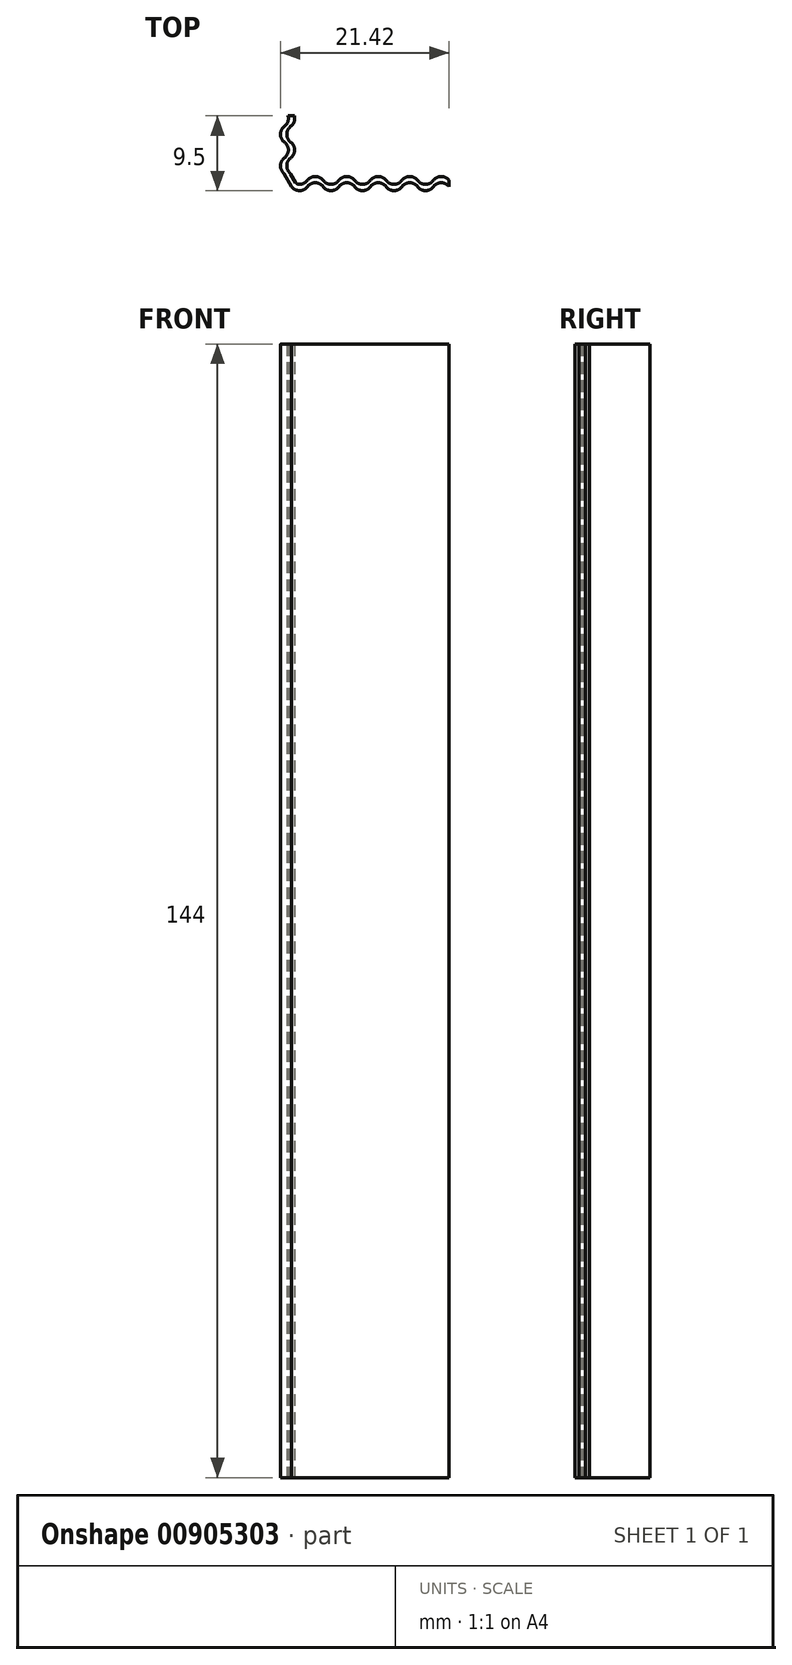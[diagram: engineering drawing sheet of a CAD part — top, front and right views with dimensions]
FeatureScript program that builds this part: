
annotation { "Feature Type Name" : "Feature", "Feature Type Description" : "" }
export const myFeature = defineFeature(function(context is Context, id is Id, definition is map)
    precondition{}
    {
        {
            var Q0;
            Q0=qCreatedBy(makeId("Top.planeOp"),FACE);
            var sketch = newSketch(context, id + "F0", { "sketchPlane" : qUnion([Q0])});
            skArc(sketch, "E0", {"start": v(-9.41, -6.92) * mm, "mid": v(-9.91, -7.92) * mm, "end": v(-9.41, -8.92) * mm});
            skArc(sketch, "E1", {"start": v(-9.41, -10.92) * mm, "mid": v(-8.91, -9.92) * mm, "end": v(-9.41, -8.92) * mm});
            skArc(sketch, "E2", {"start": v(-7.29, -13.78) * mm, "mid": v(-7.78, -14.17) * mm, "end": v(-8.4, -14.27) * mm});
            skArc(sketch, "E3", {"start": v(-8.4, -14.27) * mm, "mid": v(-8.62, -14.2) * mm, "end": v(-8.78, -14.04) * mm});
            skLineSegment(sketch, "E4", {"start": v(-8.78, -14.04) * mm, "end": v(-9.44, -12.97) * mm});
            skArc(sketch, "E5", {"start": v(-9.44, -12.97) * mm, "mid": v(-9.52, -12.85) * mm, "end": v(-9.61, -12.73) * mm});
            skArc(sketch, "E6", {"start": v(-9.61, -12.73) * mm, "mid": v(-9.9, -11.78) * mm, "end": v(-9.41, -10.92) * mm});
            skArc(sketch, "E7", {"start": v(-9.29, -14.58) * mm, "mid": v(-8.29, -15.08) * mm, "end": v(-7.29, -14.58) * mm});
            skArc(sketch, "E8", {"start": v(-5.29, -14.58) * mm, "mid": v(-6.29, -14.08) * mm, "end": v(-7.29, -14.58) * mm});
            skArc(sketch, "E9", {"start": v(-5.29, -14.58) * mm, "mid": v(-4.29, -15.08) * mm, "end": v(-3.29, -14.58) * mm});
            skArc(sketch, "E10", {"start": v(-1.29, -14.58) * mm, "mid": v(-2.29, -14.08) * mm, "end": v(-3.29, -14.58) * mm});
            skArc(sketch, "E11", {"start": v(-1.29, -14.58) * mm, "mid": v(-0.29, -15.08) * mm, "end": v(0.71, -14.58) * mm});
            skArc(sketch, "E12", {"start": v(2.71, -14.58) * mm, "mid": v(1.71, -14.08) * mm, "end": v(0.71, -14.58) * mm});
            skArc(sketch, "E13", {"start": v(10.71, -14.58) * mm, "mid": v(9.71, -14.08) * mm, "end": v(8.71, -14.58) * mm});
            skArc(sketch, "E14", {"start": v(6.71, -14.58) * mm, "mid": v(7.71, -15.08) * mm, "end": v(8.71, -14.58) * mm});
            skArc(sketch, "E15", {"start": v(6.71, -14.58) * mm, "mid": v(5.71, -14.08) * mm, "end": v(4.71, -14.58) * mm});
            skArc(sketch, "E16", {"start": v(2.71, -14.58) * mm, "mid": v(3.71, -15.08) * mm, "end": v(4.71, -14.58) * mm});
            skArc(sketch, "E17", {"start": v(-9.41, 13.08) * mm, "mid": v(-8.91, 14.08) * mm, "end": v(-9.41, 15.08) * mm});
            skArc(sketch, "E18", {"start": v(-9.41, 13.08) * mm, "mid": v(-9.91, 12.08) * mm, "end": v(-9.41, 11.08) * mm});
            skArc(sketch, "E19", {"start": v(-9.41, 9.08) * mm, "mid": v(-8.91, 10.08) * mm, "end": v(-9.41, 11.08) * mm});
            skArc(sketch, "E20", {"start": v(-9.41, 9.08) * mm, "mid": v(-9.91, 8.08) * mm, "end": v(-9.41, 7.08) * mm});
            skArc(sketch, "E21", {"start": v(-9.41, 5.08) * mm, "mid": v(-8.91, 6.08) * mm, "end": v(-9.41, 7.08) * mm});
            skArc(sketch, "E22", {"start": v(-9.41, 5.08) * mm, "mid": v(-9.91, 4.08) * mm, "end": v(-9.41, 3.08) * mm});
            skArc(sketch, "E23", {"start": v(-9.41, 1.08) * mm, "mid": v(-8.91, 2.08) * mm, "end": v(-9.41, 3.08) * mm});
            skArc(sketch, "E24", {"start": v(-9.41, 1.08) * mm, "mid": v(-9.91, 0.08) * mm, "end": v(-9.41, -0.92) * mm});
            skArc(sketch, "E25", {"start": v(-9.41, -2.92) * mm, "mid": v(-8.91, -1.92) * mm, "end": v(-9.41, -0.92) * mm});
            skArc(sketch, "E26", {"start": v(-9.41, -2.92) * mm, "mid": v(-9.91, -3.92) * mm, "end": v(-9.41, -4.92) * mm});
            skArc(sketch, "E27", {"start": v(-9.41, -6.92) * mm, "mid": v(-8.91, -5.92) * mm, "end": v(-9.41, -4.92) * mm});
            skArc(sketch, "E28", {"start": v(-10.21, -6.92) * mm, "mid": v(-10.71, -7.92) * mm, "end": v(-10.21, -8.92) * mm});
            skArc(sketch, "E29", {"start": v(-10.21, -10.92) * mm, "mid": v(-9.71, -9.92) * mm, "end": v(-10.21, -8.92) * mm});
            skLineSegment(sketch, "E30", {"start": v(-9.29, -14.58) * mm, "end": v(-10.27, -12.94) * mm});
            skArc(sketch, "E31", {"start": v(-10.27, -12.94) * mm, "mid": v(-10.35, -12.82) * mm, "end": v(-10.43, -12.7) * mm});
            skArc(sketch, "E32", {"start": v(-10.43, -12.7) * mm, "mid": v(-10.7, -11.77) * mm, "end": v(-10.21, -10.92) * mm});
            skArc(sketch, "E33", {"start": v(-5.29, -13.78) * mm, "mid": v(-6.29, -13.28) * mm, "end": v(-7.29, -13.78) * mm});
            skArc(sketch, "E34", {"start": v(-5.29, -13.78) * mm, "mid": v(-4.29, -14.28) * mm, "end": v(-3.29, -13.78) * mm});
            skArc(sketch, "E35", {"start": v(-1.29, -13.78) * mm, "mid": v(-2.29, -13.28) * mm, "end": v(-3.29, -13.78) * mm});
            skArc(sketch, "E36", {"start": v(-1.29, -13.78) * mm, "mid": v(-0.29, -14.28) * mm, "end": v(0.71, -13.78) * mm});
            skArc(sketch, "E37", {"start": v(2.71, -13.78) * mm, "mid": v(1.71, -13.28) * mm, "end": v(0.71, -13.78) * mm});
            skArc(sketch, "E38", {"start": v(10.71, -13.78) * mm, "mid": v(9.71, -13.28) * mm, "end": v(8.71, -13.78) * mm});
            skArc(sketch, "E39", {"start": v(6.71, -13.78) * mm, "mid": v(7.71, -14.28) * mm, "end": v(8.71, -13.78) * mm});
            skArc(sketch, "E40", {"start": v(6.71, -13.78) * mm, "mid": v(5.71, -13.28) * mm, "end": v(4.71, -13.78) * mm});
            skArc(sketch, "E41", {"start": v(2.71, -13.78) * mm, "mid": v(3.71, -14.28) * mm, "end": v(4.71, -13.78) * mm});
            skArc(sketch, "E42", {"start": v(-10.21, 13.08) * mm, "mid": v(-9.71, 14.08) * mm, "end": v(-10.21, 15.08) * mm});
            skArc(sketch, "E43", {"start": v(-10.21, 13.08) * mm, "mid": v(-10.71, 12.08) * mm, "end": v(-10.21, 11.08) * mm});
            skArc(sketch, "E44", {"start": v(-10.21, 9.08) * mm, "mid": v(-9.71, 10.08) * mm, "end": v(-10.21, 11.08) * mm});
            skArc(sketch, "E45", {"start": v(-10.21, 9.08) * mm, "mid": v(-10.71, 8.08) * mm, "end": v(-10.21, 7.08) * mm});
            skArc(sketch, "E46", {"start": v(-10.21, 5.08) * mm, "mid": v(-9.71, 6.08) * mm, "end": v(-10.21, 7.08) * mm});
            skArc(sketch, "E47", {"start": v(-10.21, 5.08) * mm, "mid": v(-10.71, 4.08) * mm, "end": v(-10.21, 3.08) * mm});
            skArc(sketch, "E48", {"start": v(-10.21, 1.08) * mm, "mid": v(-9.71, 2.08) * mm, "end": v(-10.21, 3.08) * mm});
            skArc(sketch, "E49", {"start": v(-10.21, 1.08) * mm, "mid": v(-10.71, 0.08) * mm, "end": v(-10.21, -0.92) * mm});
            skArc(sketch, "E50", {"start": v(-10.21, -2.92) * mm, "mid": v(-9.71, -1.92) * mm, "end": v(-10.21, -0.92) * mm});
            skArc(sketch, "E51", {"start": v(-10.21, -2.92) * mm, "mid": v(-10.71, -3.92) * mm, "end": v(-10.21, -4.92) * mm});
            skArc(sketch, "E52", {"start": v(-10.21, -6.92) * mm, "mid": v(-9.71, -5.92) * mm, "end": v(-10.21, -4.92) * mm});
            skLineSegment(sketch, "E53", {"start": v(10.71, -13.78) * mm, "end": v(10.71, -14.58) * mm});
            skLineSegment(sketch, "E54", {"start": v(10.71, -2.58) * mm, "end": v(-10.29, -2.58) * mm});
            skLineSegment(sketch, "E55", {"start": v(-8.4, -14.27) * mm, "end": v(-8.66, -2.58) * mm, "construction": true});
            skLineSegment(sketch, "E56.0", {"start": v(10.71, 2.42) * mm, "end": v(-10.29, 2.42) * mm});
            skLineSegment(sketch, "E57.0", {"start": v(10.71, -5.58) * mm, "end": v(-10.29, -5.58) * mm});
            skLineSegment(sketch, "E58", {"start": v(-10.29, -5.58) * mm, "end": v(-10.82, -5.58) * mm});
            skSolve(sketch);
        }
        {
            var Q0;
            {var subQ4=sQuery(id+"F0.wireOp",EDGE,"E1");Q0=makeQuery(id+"F0.imprint","IMPRINT",FACE,{"disambiguationData":[TD([[makeQuery(id+"F0.imprint","IMPRINT",EDGE,{"derivedFrom":subQ4}),1.0]])]});}
            extrude(context, id + "F1", {"entities" : qUnion([Q0]), "depth" : 144 * mm, "offsetDistance" : 25 * mm});
        }
    });
